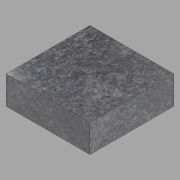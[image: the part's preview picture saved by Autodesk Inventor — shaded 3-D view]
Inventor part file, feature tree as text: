
AUTODESK INVENTOR PART (.ipt)
format: ipt  version: 2022.2 (Build 262287000, 287)  size: 115,712 bytes
history: native  units: in
note: dims shown in document units (in); Inventor stores cm internally (conversion verified against a paired STEP export)
features: extrude x1, sketch x1
ambient origin geometry x8: Origin, YZ Plane, XZ Plane, XY Plane, X Axis, Y Axis, Z Axis, Center Point
bodies: Solid1 (feature_tree)
feature tree (2):
  extrude  "Extrusion1"  Depth=18.0in
  sketch  "Sketch1"  dims[d0=18.0in d1=18.0in d2=6.0in d3=0.0in]
